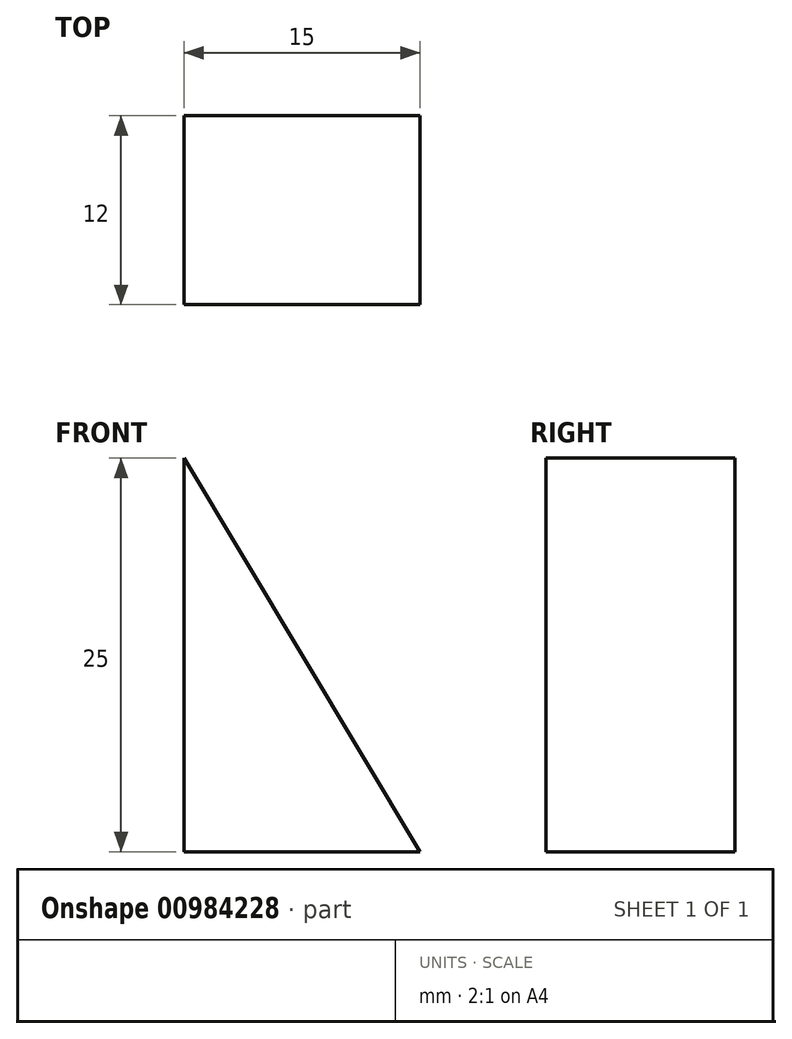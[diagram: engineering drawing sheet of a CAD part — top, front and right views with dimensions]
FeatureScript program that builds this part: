
annotation { "Feature Type Name" : "Feature", "Feature Type Description" : "" }
export const myFeature = defineFeature(function(context is Context, id is Id, definition is map)
    precondition{}
    {
        {
            var Q0;
            Q0=qCreatedBy(makeId("Front.planeOp"),FACE);
            var sketch = newSketch(context, id + "F0", { "sketchPlane" : qUnion([Q0])});
            skLineSegment(sketch, "E0", {"start": v(0, 0) * mm, "end": v(0, 25) * mm});
            skLineSegment(sketch, "E1", {"start": v(0, 25) * mm, "end": v(15, 0) * mm});
            skLineSegment(sketch, "E2", {"start": v(15, 0) * mm, "end": v(0, 0) * mm});
            skSolve(sketch);
        }
        {
            var Q0;
            Q0=makeQuery(id+"F0.imprint","IMPRINT",FACE,{"disambiguationData":[TD([[makeQuery(id+"F0.imprint","IMPRINT",EDGE,{"derivedFrom":sQuery(id+"F0.wireOp",EDGE,"E0")}),-1.0]])]});
            extrude(context, id + "F1", {"entities" : qUnion([Q0]), "oppositeDirection" : true, "depth" : 12 * mm, "offsetDistance" : 25 * mm});
        }
    });
